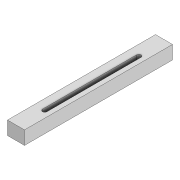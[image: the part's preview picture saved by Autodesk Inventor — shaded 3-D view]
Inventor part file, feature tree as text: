
AUTODESK INVENTOR PART (.ipt)
format: ipt  version: 2022 (Build 260153000, 153)  size: 88,064 bytes
history: native  units: mm
features: extrude x1, sketch x1
ambient origin geometry x8: Origin, YZ Plane, XZ Plane, XY Plane, X Axis, Y Axis, Z Axis, Center Point
bodies: Solid1 (feature_tree)
feature tree (2):
  extrude  "Extrusion1"  Depth=70.0mm
  sketch  "Sketch1"  dims[d0=3.3mm d1=70.0mm d2=10.0mm d3=10.0mm d4=20.0mm d5=20.0mm d6=6.0mm d7=10.0mm d8=0.0mm]
